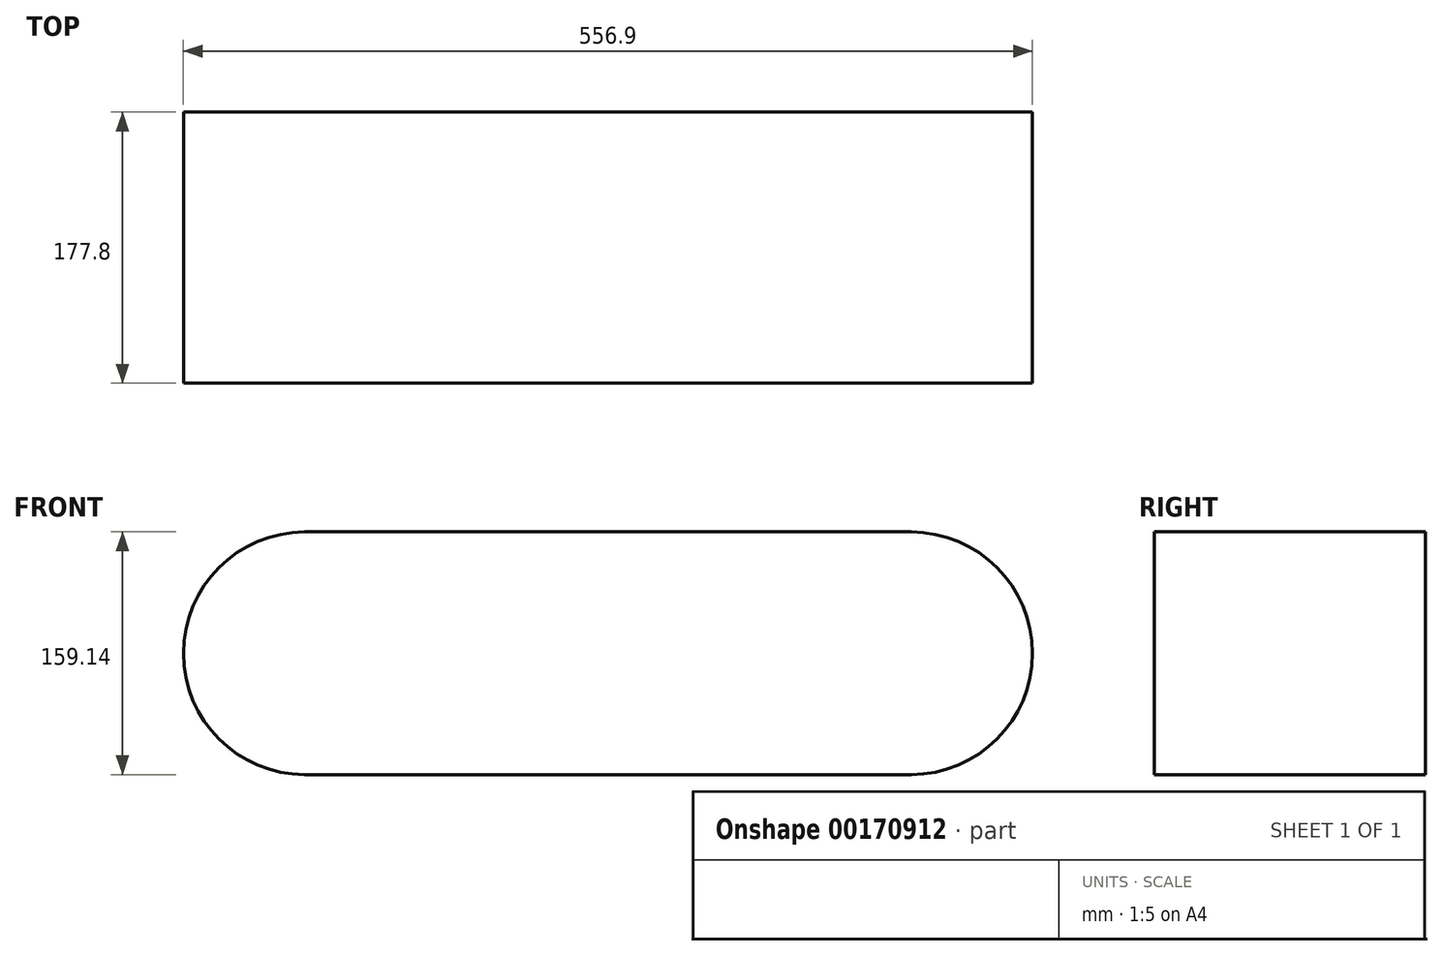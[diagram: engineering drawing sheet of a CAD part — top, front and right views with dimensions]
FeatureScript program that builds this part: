
annotation { "Feature Type Name" : "Feature", "Feature Type Description" : "" }
export const myFeature = defineFeature(function(context is Context, id is Id, definition is map)
    precondition{}
    {
        {
            var Q0;
            Q0=qCreatedBy(makeId("Front.planeOp"),FACE);
            var sketch = newSketch(context, id + "F0", { "sketchPlane" : qUnion([Q0])});
            skLineSegment(sketch, "E0.bottom", {"start": v(198.88, -79.57) * mm, "end": v(-198.88, -79.57) * mm});
            skLineSegment(sketch, "E0.top", {"start": v(198.88, 79.57) * mm, "end": v(-198.88, 79.57) * mm});
            skPoint(sketch, "E0.middle", {"position": v(0, 0) * mm});
            skArc(sketch, "E1", {"start": v(-198.88, 79.57) * mm, "mid": v(-278.45, 0) * mm, "end": v(-198.88, -79.57) * mm});
            skArc(sketch, "E2", {"start": v(198.88, 79.57) * mm, "mid": v(278.45, 0) * mm, "end": v(198.88, -79.57) * mm});
            skSolve(sketch);
        }
        {
            var Q0;
            Q0 = qSketchRegion(id + "F0", true);
            extrude(context, id + "F1", {"entities" : qUnion([Q0]), "depth" : 177.8 * mm});
        }
    });
